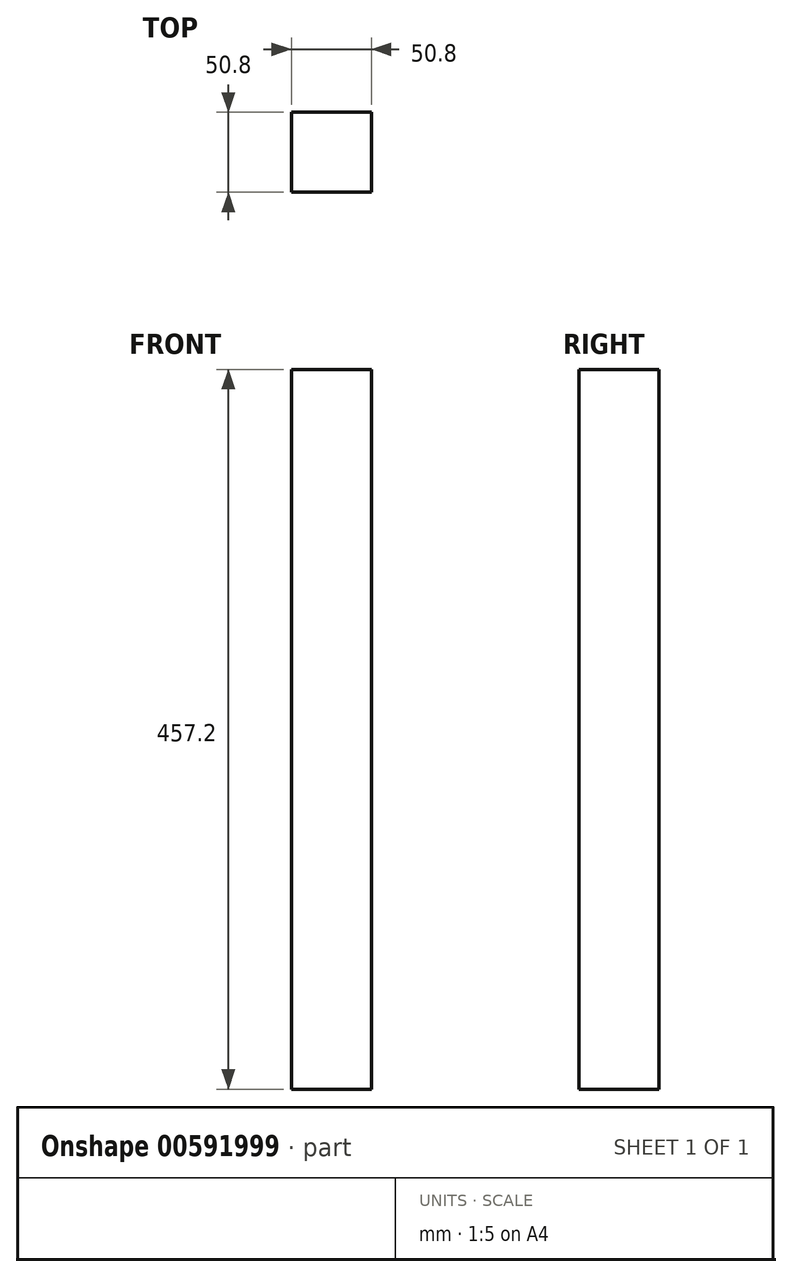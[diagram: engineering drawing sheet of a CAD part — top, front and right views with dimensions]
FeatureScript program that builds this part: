
annotation { "Feature Type Name" : "Feature", "Feature Type Description" : "" }
export const myFeature = defineFeature(function(context is Context, id is Id, definition is map)
    precondition{}
    {
        {
            var Q0;
            Q0=qCreatedBy(makeId("Top.planeOp"),FACE);
            var sketch = newSketch(context, id + "F0", { "sketchPlane" : qUnion([Q0])});
            skLineSegment(sketch, "E0.bottom", {"start": v(-20.39, 59.13) * mm, "end": v(30.41, 59.13) * mm});
            skLineSegment(sketch, "E0.top", {"start": v(-20.39, 8.33) * mm, "end": v(30.41, 8.33) * mm});
            skLineSegment(sketch, "E0.left", {"start": v(-20.39, 59.13) * mm, "end": v(-20.39, 8.33) * mm});
            skLineSegment(sketch, "E0.right", {"start": v(30.41, 59.13) * mm, "end": v(30.41, 8.33) * mm});
            skSolve(sketch);
        }
        {
            var Q0;
            Q0 = qSketchRegion(id + "F0", true);
            extrude(context, id + "F1", {"entities" : qUnion([Q0]), "endBound" : BoundingType.SYMMETRIC, "oppositeDirection" : true, "depth" : 457.2 * mm, "offsetDistance" : 25.4 * mm});
        }
    });
